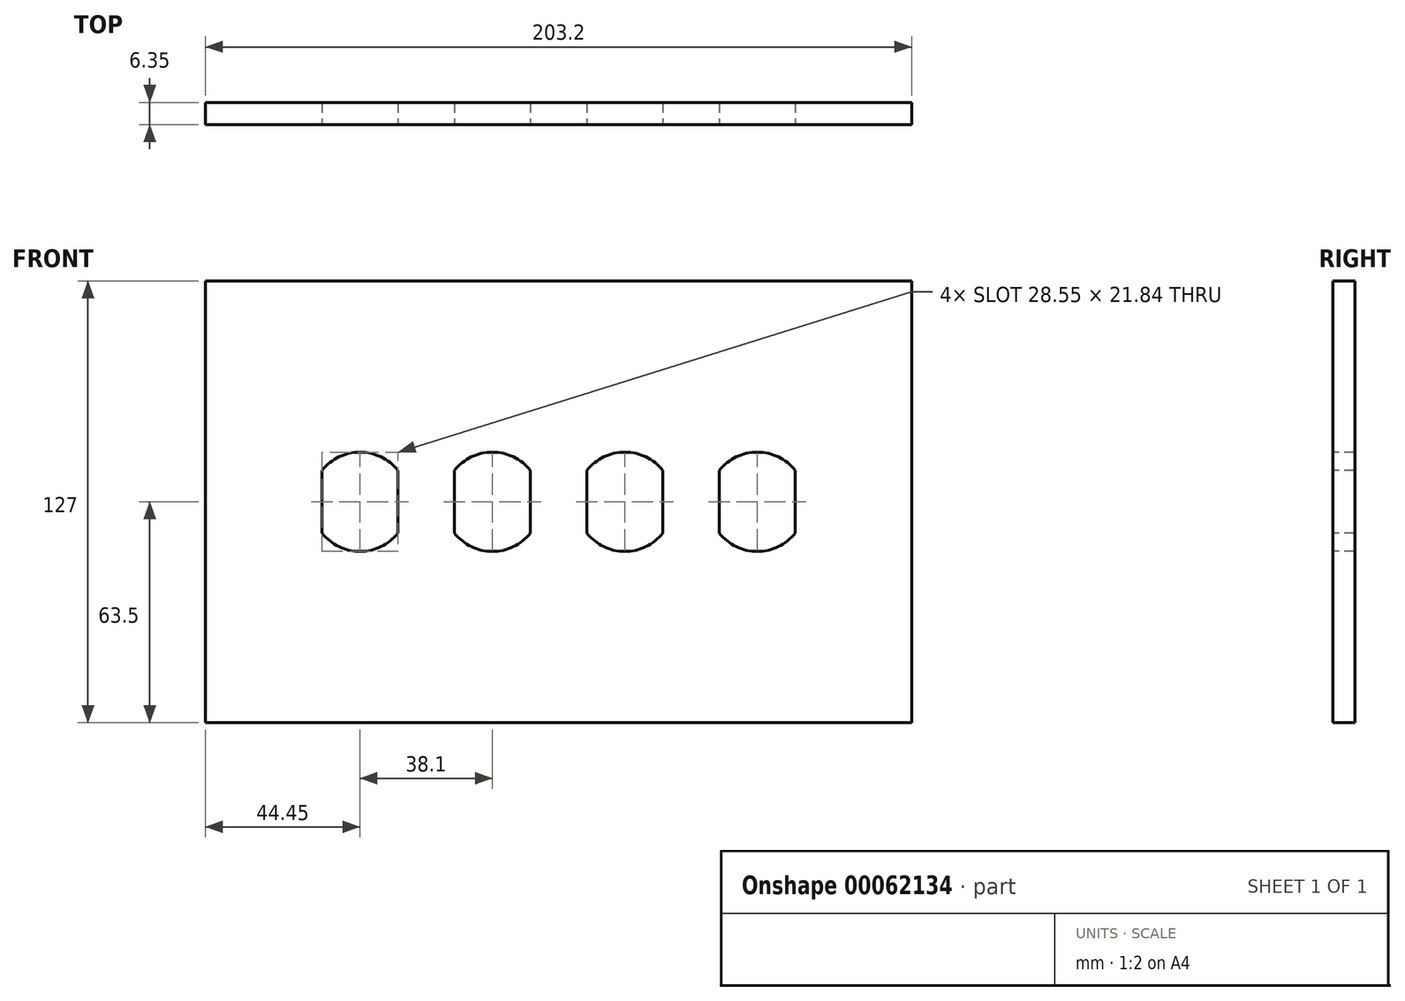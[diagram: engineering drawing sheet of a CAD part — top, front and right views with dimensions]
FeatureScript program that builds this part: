
annotation { "Feature Type Name" : "Feature", "Feature Type Description" : "" }
export const myFeature = defineFeature(function(context is Context, id is Id, definition is map)
    precondition{}
    {
        {
            var Q0;
            Q0=qCreatedBy(makeId("Front.planeOp"),FACE);
            var sketch = newSketch(context, id + "F0", { "sketchPlane" : qUnion([Q0])});
            skLineSegment(sketch, "E0.rect.bottom", {"start": v(101.6, 63.5) * mm, "end": v(-101.6, 63.5) * mm});
            skLineSegment(sketch, "E0.rect.top", {"start": v(101.6, -63.5) * mm, "end": v(-101.6, -63.5) * mm});
            skLineSegment(sketch, "E0.rect.left", {"start": v(101.6, 63.5) * mm, "end": v(101.6, -63.5) * mm});
            skLineSegment(sketch, "E0.rect.right", {"start": v(-101.6, 63.5) * mm, "end": v(-101.6, -63.5) * mm});
            skPoint(sketch, "E0.rect.middle", {"position": v(0, 0) * mm});
            skSolve(sketch);
        }
        {
            var Q0;
            Q0 = qSketchRegion(id + "F0", true);
            extrude(context, id + "F1", {"entities" : qUnion([Q0]), "depth" : 6.35 * mm});
        }
        {
            var Q0;
            Q0=makeQuery(id+"F1.opExtrude","CAP_FACE",FACE,{"disambiguationData":[OSD([sQuery(id+"F0.wireOp",EDGE,"E0.rect.bottom"),sQuery(id+"F0.wireOp",EDGE,"E0.rect.top"),sQuery(id+"F0.wireOp",EDGE,"E0.rect.left"),sQuery(id+"F0.wireOp",EDGE,"E0.rect.right")])],"isStart":false});
            var sketch = newSketch(context, id + "F2", { "sketchPlane" : qUnion([Q0])});
            skLineSegment(sketch, "E1", {"start": v(-68.07, 0) * mm, "end": v(-68.07, 9.02) * mm});
            skLineSegment(sketch, "E2", {"start": v(-46.23, 0) * mm, "end": v(-46.23, 9.02) * mm});
            skArc(sketch, "E3", {"start": v(-46.23, 9.02) * mm, "mid": v(-57.15, 14.28) * mm, "end": v(-68.07, 9.02) * mm});
            skLineSegment(sketch, "E4.MirrorCS", {"start": v(-68.07, 0) * mm, "end": v(-68.07, -9.02) * mm});
            skLineSegment(sketch, "E5.MirrorCS", {"start": v(-46.23, 0) * mm, "end": v(-46.23, -9.02) * mm});
            skArc(sketch, "E6.MirrorCS", {"start": v(-46.23, -9.02) * mm, "mid": v(-57.15, -14.28) * mm, "end": v(-68.07, -9.02) * mm});
            skLineSegment(sketch, "E7.1.0.0", {"start": v(-29.97, 0) * mm, "end": v(-29.97, 9.02) * mm});
            skLineSegment(sketch, "E7.1.0.1", {"start": v(-29.97, 0) * mm, "end": v(-29.97, -9.02) * mm});
            skLineSegment(sketch, "E7.1.0.2", {"start": v(-8.13, 0) * mm, "end": v(-8.13, 9.02) * mm});
            skLineSegment(sketch, "E7.1.0.3", {"start": v(-8.13, 0) * mm, "end": v(-8.13, -9.02) * mm});
            skArc(sketch, "E7.1.0.4", {"start": v(-8.13, 9.02) * mm, "mid": v(-19.05, 14.28) * mm, "end": v(-29.97, 9.02) * mm});
            skArc(sketch, "E7.1.0.5", {"start": v(-8.13, -9.02) * mm, "mid": v(-19.05, -14.28) * mm, "end": v(-29.97, -9.02) * mm});
            skLineSegment(sketch, "E7.2.0.0", {"start": v(8.13, 0) * mm, "end": v(8.13, 9.02) * mm});
            skLineSegment(sketch, "E7.2.0.1", {"start": v(8.13, 0) * mm, "end": v(8.13, -9.02) * mm});
            skLineSegment(sketch, "E7.2.0.2", {"start": v(29.97, 0) * mm, "end": v(29.97, 9.02) * mm});
            skLineSegment(sketch, "E7.2.0.3", {"start": v(29.97, 0) * mm, "end": v(29.97, -9.02) * mm});
            skArc(sketch, "E7.2.0.4", {"start": v(29.97, 9.02) * mm, "mid": v(19.05, 14.28) * mm, "end": v(8.13, 9.02) * mm});
            skArc(sketch, "E7.2.0.5", {"start": v(29.97, -9.02) * mm, "mid": v(19.05, -14.28) * mm, "end": v(8.13, -9.02) * mm});
            skLineSegment(sketch, "E7.3.0.0", {"start": v(46.23, 0) * mm, "end": v(46.23, 9.02) * mm});
            skLineSegment(sketch, "E7.3.0.1", {"start": v(46.23, 0) * mm, "end": v(46.23, -9.02) * mm});
            skLineSegment(sketch, "E7.3.0.2", {"start": v(68.07, 0) * mm, "end": v(68.07, 9.02) * mm});
            skLineSegment(sketch, "E7.3.0.3", {"start": v(68.07, 0) * mm, "end": v(68.07, -9.02) * mm});
            skArc(sketch, "E7.3.0.4", {"start": v(68.07, 9.02) * mm, "mid": v(57.15, 14.28) * mm, "end": v(46.23, 9.02) * mm});
            skArc(sketch, "E7.3.0.5", {"start": v(68.07, -9.02) * mm, "mid": v(57.15, -14.28) * mm, "end": v(46.23, -9.02) * mm});
            skLineSegment(sketch, "E7.direction1", {"start": v(-68.07, -9.02) * mm, "end": v(-29.97, -9.02) * mm, "construction": true});
            skSolve(sketch);
        }
        {
            var Q0;
            Q0 = qSketchRegion(id + "F2", true);
            extrude(context, id + "F3", {"entities" : qUnion([Q0]), "operationType" : NewBodyOperationType.REMOVE, "endBound" : BoundingType.UP_TO_NEXT, "oppositeDirection" : true, "depth" : 25.4 * mm});
        }
    });
